# Revit family: AFX-Indra-Linear_Pendanat
name_source: partatom
category: Lighting Fixtures
units: mm (PartAtom-declared; Revit-internal decimal feet)

## family parameters
Cut with Voids When Loaded = No
Host = Face
Light Source = No
Part Type = Normal
Room Calculation Point = No
Round Connector Dimension = Use Diameter
Shared = No

## types (1)
- IDRP0344LAJUDBK
    Apparent Load = 0 VA
    Assembly Code = D5020200
    Colour Rendering Index = 80
    Cord Finish = AFX - Black Steel
    Cover Finish = AFX - Black Steel
    Default Elevation = 48"
    Description = Linear Pendant - 44 1/4"L x 3"W x 3"H
    Diffuser Finish = AFX - White Acrylic
    Height = 3"
    Housing Finish = AFX - Black Steel
    Keynote = 12500
    Length = 44 1/4"
    Manufacturer = AFX Inc
    Model = IDRP0344LAJUDBK
    Power Factor = 1
    Product Documentation Link = https://www.afxinc.com
    Revit File Built By = https://servex-us.com
    Supports Finish = AFX - Black Steel
    Sustainability = https://lamprecycle.org
    Type Comments = Indra
    URL = https://www.afxinc.com
    Voltage = 120 V
    Wattage Comments = 9
    Width = 3"

## geometry (parser evidence)
native form markers: Sweep x8
no freeform markers — native parametric forms only
